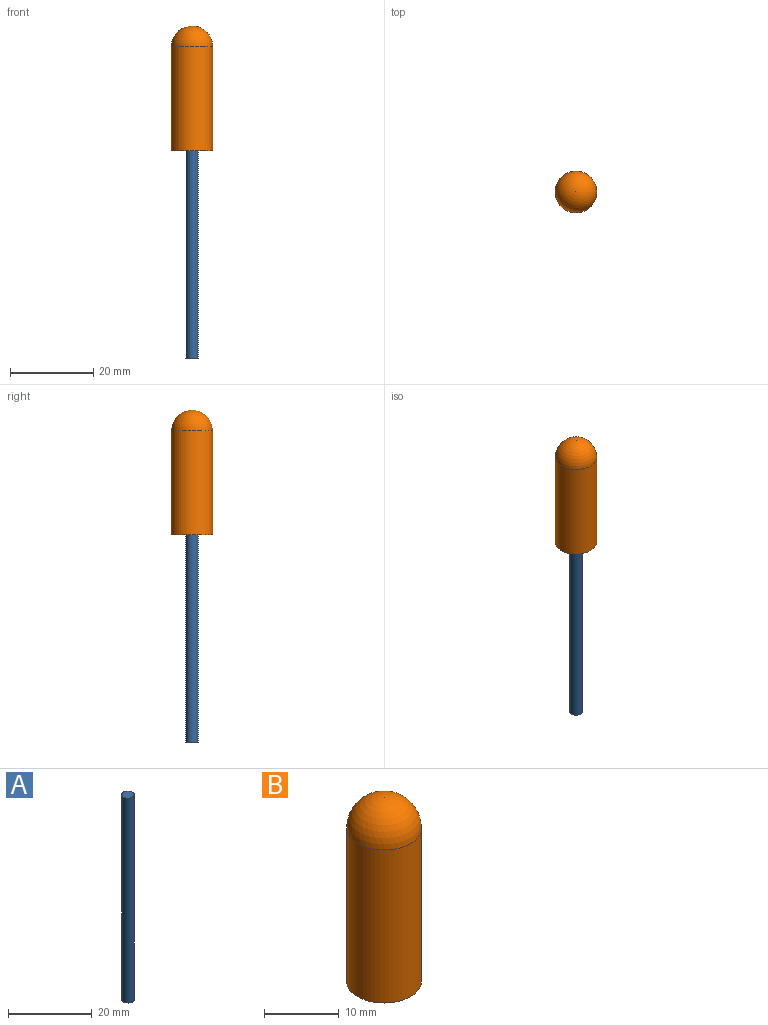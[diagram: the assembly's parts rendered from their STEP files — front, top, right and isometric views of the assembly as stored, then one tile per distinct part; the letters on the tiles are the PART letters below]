
ASSEMBLY  parts=2 mates=1
PART A: 3 faces, bbox 3x3x60 mm
  f0: cylinder r=1.5mm len=60mm, axis (0,0,1), area 565.5mm2, adj f1,f2
  f1: plane 3x3mm, normal (0,0,-1), area 7.1mm2, adj f0
  f2: plane 3x3mm, normal (0,0,1), area 7.1mm2, adj f0
PART B: 5 faces, bbox 10x10x30 mm
  f0: cylinder r=5mm len=25mm, axis (0,0,1), area 785.4mm2, adj f1,f4
  f1: plane 10x10mm, normal (0,0,-1), area 71.5mm2, adj f0,f2
  f2: cylinder r=1.5mm len=10mm, axis (0,0,1), area 94.2mm2, adj f1,f3
  f3: plane 3x3mm, normal (0,0,-1), area 7.1mm2, adj f2
  f4: sphere r=5mm, area 157.1mm2, adj f0
PLACE A t=(20.8,-227.51,110.05)mm fixed
PLACE B t=(20.8,-227.51,110.05)mm
MATE fastened B.f0 <-> A.f0  axis (0,0,-1) through (15.8,112.49,185.05)mm
